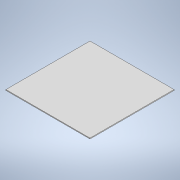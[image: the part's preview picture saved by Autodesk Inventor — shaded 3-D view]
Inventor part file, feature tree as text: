
AUTODESK INVENTOR PART (.ipt)
format: ipt  version: 2020 (Build 240168000, 168)  size: 91,648 bytes
history: native  units: mm
features: other x1, extrude x1, sketch x1
ambient origin geometry x8: Origin, YZ Plane, XZ Plane, XY Plane, X Axis, Y Axis, Z Axis, Center Point
bodies: Body1 (feature_tree)
feature tree (3):
  other  "Bryła1"
  extrude  "Wyciągnięcie proste1"  Depth=100.0mm
  sketch  "Szkic1"
